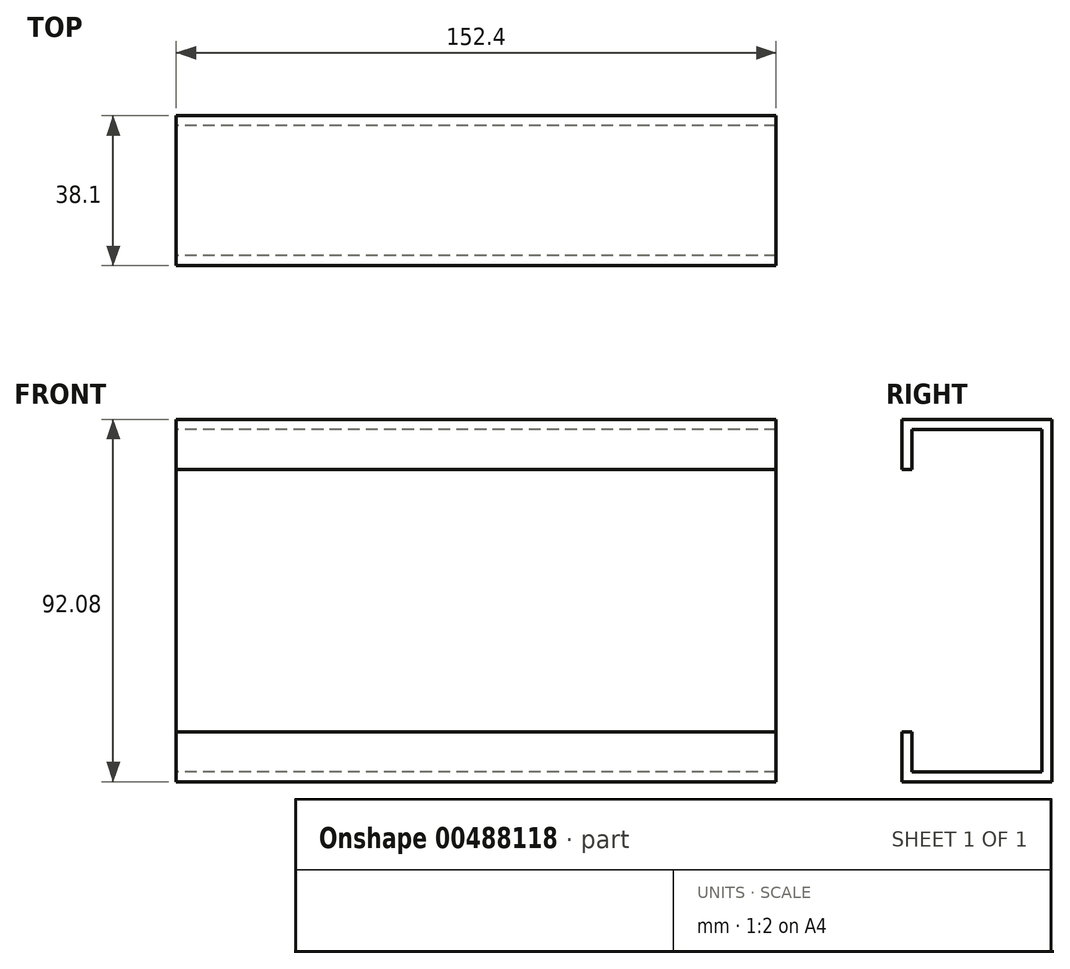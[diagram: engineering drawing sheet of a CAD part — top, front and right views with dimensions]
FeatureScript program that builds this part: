
annotation { "Feature Type Name" : "Feature", "Feature Type Description" : "" }
export const myFeature = defineFeature(function(context is Context, id is Id, definition is map)
    precondition{}
    {
        {
            var Q0;
            Q0=qCreatedBy(makeId("Right.planeOp"),FACE);
            var sketch = newSketch(context, id + "F0", { "sketchPlane" : qUnion([Q0])});
            skLineSegment(sketch, "E0", {"start": v(-13.12, 33.34) * mm, "end": v(-13.12, 46.04) * mm});
            skLineSegment(sketch, "E1", {"start": v(-13.12, 46.04) * mm, "end": v(24.98, 46.04) * mm});
            skLineSegment(sketch, "E2", {"start": v(24.98, 46.04) * mm, "end": v(24.98, -46.04) * mm});
            skLineSegment(sketch, "E3", {"start": v(24.98, -46.04) * mm, "end": v(-13.12, -46.04) * mm});
            skLineSegment(sketch, "E4", {"start": v(-13.12, -46.04) * mm, "end": v(-13.12, -33.34) * mm});
            skLineSegment(sketch, "E5.0", {"start": v(-10.58, -43.5) * mm, "end": v(-10.58, -33.34) * mm});
            skLineSegment(sketch, "E5.1", {"start": v(-10.58, 33.34) * mm, "end": v(-10.58, 43.5) * mm});
            skLineSegment(sketch, "E5.2", {"start": v(-10.58, 43.5) * mm, "end": v(22.44, 43.5) * mm});
            skLineSegment(sketch, "E5.3", {"start": v(22.44, 43.5) * mm, "end": v(22.44, -43.5) * mm});
            skLineSegment(sketch, "E5.4", {"start": v(22.44, -43.5) * mm, "end": v(-10.58, -43.5) * mm});
            skLineSegment(sketch, "E6", {"start": v(-13.12, 33.34) * mm, "end": v(-10.58, 33.34) * mm});
            skLineSegment(sketch, "E7", {"start": v(-13.12, -33.34) * mm, "end": v(-10.58, -33.34) * mm});
            skSolve(sketch);
        }
        {
            var Q0;
            Q0=makeQuery(id+"F0.imprint","IMPRINT",FACE,{"disambiguationData":[TD([[makeQuery(id+"F0.imprint","IMPRINT",EDGE,{"derivedFrom":sQuery(id+"F0.wireOp",EDGE,"E0")}),-1.0]])]});
            extrude(context, id + "F1", {"entities" : qUnion([Q0]), "depth" : 152.4 * mm});
        }
    });
